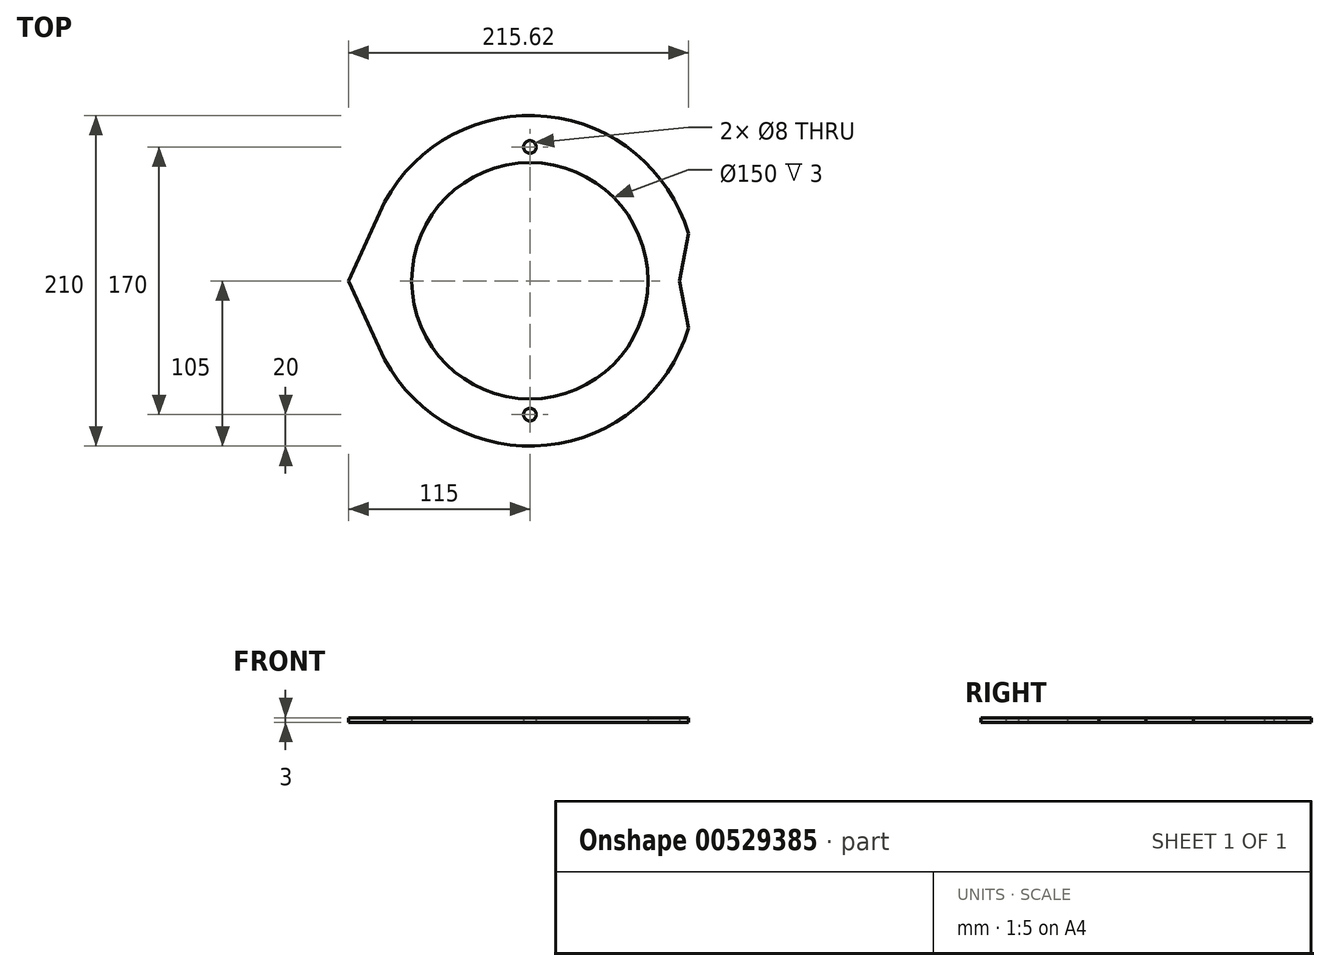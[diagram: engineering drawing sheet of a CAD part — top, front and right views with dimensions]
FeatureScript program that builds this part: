
annotation { "Feature Type Name" : "Feature", "Feature Type Description" : "" }
export const myFeature = defineFeature(function(context is Context, id is Id, definition is map)
    precondition{}
    {
        {
            var Q0;
            Q0=qCreatedBy(makeId("Top.planeOp"),FACE);
            var sketch = newSketch(context, id + "F0", { "sketchPlane" : qUnion([Q0])});
            skCircle(sketch, "E0", {"center": v(0, 0) * mm, "radius": 75 * mm});
            skArc(sketch, "E1.0", {"start": v(-92.33, -50) * mm, "mid": v(10.83, -104.44) * mm, "end": v(100.62, -30) * mm});
            skLineSegment(sketch, "E2", {"start": v(-115, 0) * mm, "end": v(-92.33, 50) * mm});
            skLineSegment(sketch, "E3", {"start": v(-92.33, -50) * mm, "end": v(-115, 0) * mm});
            skLineSegment(sketch, "E4", {"start": v(95, 0) * mm, "end": v(100.62, 30) * mm});
            skLineSegment(sketch, "E5", {"start": v(100.62, -30) * mm, "end": v(95, 0) * mm});
            skArc(sketch, "E6.trimOffspring", {"start": v(100.62, 30) * mm, "mid": v(10.83, 104.44) * mm, "end": v(-92.33, 50) * mm});
            skCircle(sketch, "E7", {"center": v(0, 85) * mm, "radius": 4 * mm});
            skCircle(sketch, "E8", {"center": v(0, -85) * mm, "radius": 4 * mm});
            skLineSegment(sketch, "E9", {"start": v(-115, 0) * mm, "end": v(-90, 0) * mm});
            skPoint(sketch, "E10", {"position": v(-85, 0) * mm});
            skPoint(sketch, "E11", {"position": v(-90, 0) * mm});
            skArc(sketch, "E12", {"start": v(-85, 0) * mm, "mid": v(-87.5, 9.33) * mm, "end": v(-90, 0) * mm});
            skPoint(sketch, "E13", {"position": v(85, 0) * mm});
            skPoint(sketch, "E14", {"position": v(90, 0) * mm});
            skLineSegment(sketch, "E15", {"start": v(75, 0) * mm, "end": v(85, 0) * mm});
            skLineSegment(sketch, "E16.trimOffspring", {"start": v(-85, 0) * mm, "end": v(-75, 0) * mm, "construction": true});
            skArc(sketch, "E17", {"start": v(85, 0) * mm, "mid": v(87.5, -9.33) * mm, "end": v(90, 0) * mm});
            skLineSegment(sketch, "E18.trimOffspring", {"start": v(90, 0) * mm, "end": v(95, 0) * mm, "construction": true});
            skLineSegment(sketch, "E19.trimOffspring", {"start": v(90, 0) * mm, "end": v(95, 0) * mm});
            skLineSegment(sketch, "E20.trimOffspring", {"start": v(-85, 0) * mm, "end": v(-75, 0) * mm});
            skLineSegment(sketch, "E21.trimOffspring", {"start": v(75, 0) * mm, "end": v(85, 0) * mm, "construction": true});
            skPoint(sketch, "E22.orphan", {"position": v(-130.3, 0) * mm});
            skLineSegment(sketch, "E23", {"start": v(80, 0) * mm, "end": v(85, 0) * mm, "construction": true});
            skPoint(sketch, "E23.endSnap0", {"position": v(80, 0) * mm});
            skPoint(sketch, "E24.orphan", {"position": v(162.95, 0) * mm});
            skSolve(sketch);
        }
        {
            var Q0;
            Q0 = qSketchRegion(id + "F0", true);
            extrude(context, id + "F1", {"entities" : qUnion([Q0]), "depth" : 3 * mm, "offsetDistance" : 25 * mm});
        }
    });
